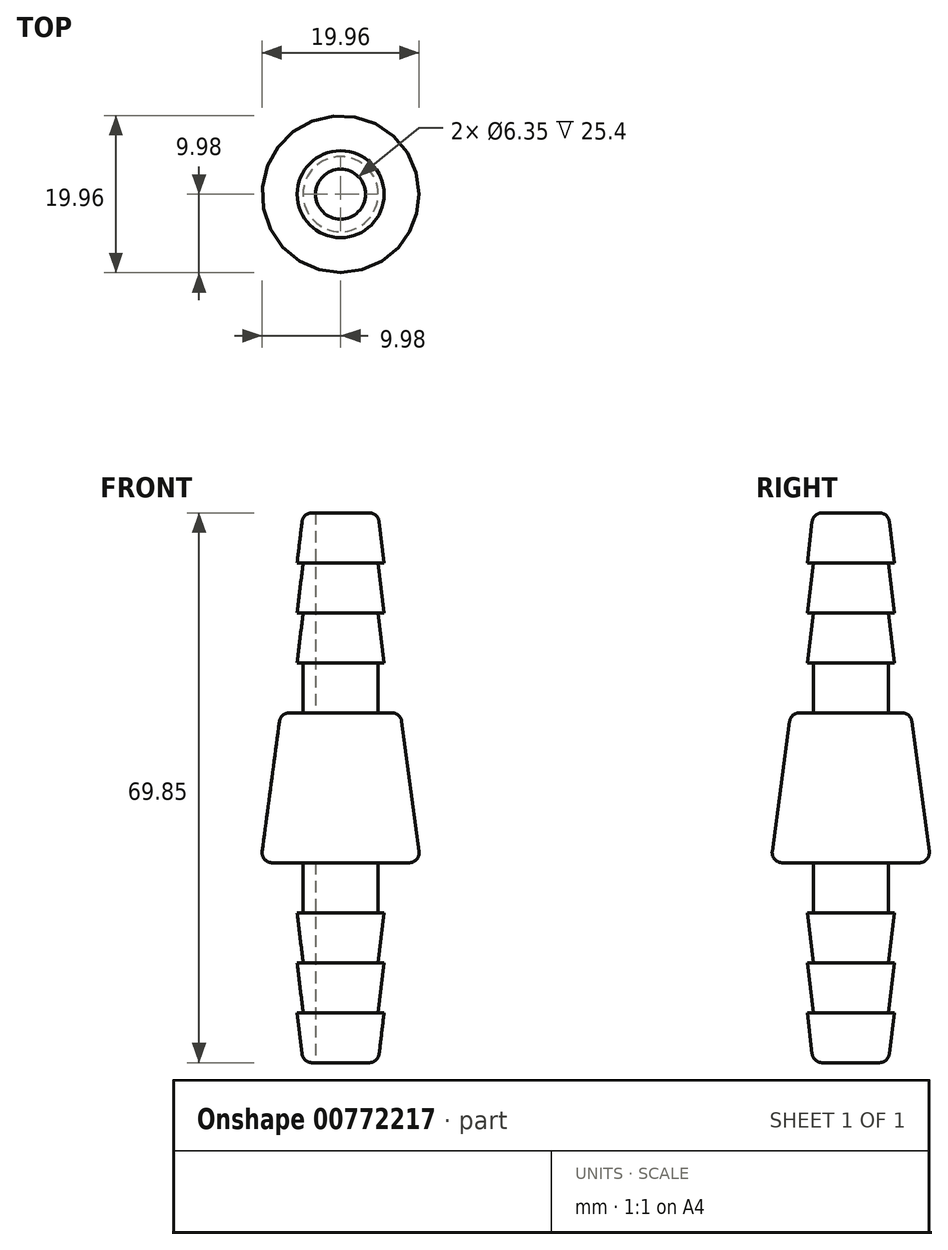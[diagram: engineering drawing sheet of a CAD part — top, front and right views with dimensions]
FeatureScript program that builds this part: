
annotation { "Feature Type Name" : "Feature", "Feature Type Description" : "" }
export const myFeature = defineFeature(function(context is Context, id is Id, definition is map)
    precondition{}
    {
        {
            var Q0;
            Q0=qCreatedBy(makeId("Front.planeOp"),FACE);
            var sketch = newSketch(context, id + "F0", { "sketchPlane" : qUnion([Q0])});
            skLineSegment(sketch, "E0", {"start": v(0, 0) * mm, "end": v(0, 69.85) * mm});
            skLineSegment(sketch, "E1", {"start": v(0, 34.93) * mm, "end": v(8.89, 34.93) * mm});
            skLineSegment(sketch, "E2", {"start": v(8.9, 34.93) * mm, "end": v(7.62, 44.45) * mm});
            skLineSegment(sketch, "E3", {"start": v(7.62, 44.45) * mm, "end": v(4.76, 44.45) * mm});
            skLineSegment(sketch, "E4", {"start": v(8.89, 34.93) * mm, "end": v(10.16, 25.4) * mm});
            skLineSegment(sketch, "E5", {"start": v(10.16, 25.4) * mm, "end": v(0, 25.4) * mm});
            skLineSegment(sketch, "E6", {"start": v(0, 44.45) * mm, "end": v(3.17, 44.45) * mm});
            skLineSegment(sketch, "E7", {"start": v(4.76, 44.45) * mm, "end": v(5.52, 44.45) * mm});
            skLineSegment(sketch, "E8", {"start": v(3.17, 44.45) * mm, "end": v(3.17, 69.85) * mm});
            skLineSegment(sketch, "E9", {"start": v(4.76, 44.45) * mm, "end": v(4.76, 50.8) * mm});
            skLineSegment(sketch, "E10", {"start": v(3.17, 69.85) * mm, "end": v(5.52, 69.85) * mm});
            skLineSegment(sketch, "E11", {"start": v(4.76, 50.8) * mm, "end": v(5.52, 50.8) * mm});
            skLineSegment(sketch, "E12", {"start": v(5.52, 50.8) * mm, "end": v(4.76, 57.15) * mm});
            skLineSegment(sketch, "E13", {"start": v(4.76, 57.15) * mm, "end": v(5.52, 57.15) * mm});
            skLineSegment(sketch, "E14", {"start": v(5.52, 57.15) * mm, "end": v(4.76, 63.5) * mm});
            skLineSegment(sketch, "E15", {"start": v(4.76, 63.5) * mm, "end": v(5.52, 63.5) * mm});
            skLineSegment(sketch, "E16", {"start": v(5.52, 63.5) * mm, "end": v(4.76, 69.85) * mm});
            skLineSegment(sketch, "E17.trimOffspring", {"start": v(3.17, 44.45) * mm, "end": v(0, 44.45) * mm});
            skLineSegment(sketch, "E18.MirrorCS", {"start": v(0, 25.4) * mm, "end": v(3.17, 25.4) * mm});
            skLineSegment(sketch, "E19.MirrorCS", {"start": v(4.76, 25.4) * mm, "end": v(5.52, 25.4) * mm});
            skLineSegment(sketch, "E20.MirrorCS", {"start": v(7.62, 25.4) * mm, "end": v(4.76, 25.4) * mm});
            skLineSegment(sketch, "E21.MirrorCS", {"start": v(3.17, 25.4) * mm, "end": v(0, 25.4) * mm});
            skLineSegment(sketch, "E22.MirrorCS", {"start": v(4.76, 19.05) * mm, "end": v(5.52, 19.05) * mm});
            skLineSegment(sketch, "E23.MirrorCS", {"start": v(3.17, 0) * mm, "end": v(5.52, 0) * mm});
            skLineSegment(sketch, "E24.MirrorCS", {"start": v(4.76, 6.35) * mm, "end": v(5.52, 6.35) * mm});
            skLineSegment(sketch, "E25.MirrorCS", {"start": v(4.76, 12.7) * mm, "end": v(5.52, 12.7) * mm});
            skLineSegment(sketch, "E26.MirrorCS", {"start": v(4.76, 25.4) * mm, "end": v(4.76, 19.05) * mm});
            skLineSegment(sketch, "E27.MirrorCS", {"start": v(3.17, 25.4) * mm, "end": v(3.17, 0) * mm});
            skLineSegment(sketch, "E28.MirrorCS", {"start": v(5.52, 12.7) * mm, "end": v(4.76, 6.35) * mm});
            skLineSegment(sketch, "E29.MirrorCS", {"start": v(5.52, 6.35) * mm, "end": v(4.76, 0) * mm});
            skLineSegment(sketch, "E30.MirrorCS", {"start": v(5.52, 19.05) * mm, "end": v(4.76, 12.7) * mm});
            skSolve(sketch);
        }
        {
            var Q0;
            Q0 = qSketchRegion(id + "F0", true);
            var Q1;
            Q1=sQuery(id+"F0.wireOp",EDGE,"E0");
            revolve(context, id + "F1", {"surfaceOperationType" : NewSurfaceOperationType.NEW, "entities" : qUnion([Q0]), "axis" : qUnion([Q1]), "revolveType" : RevolveType.FULL});
        }
        {
            var Q0;
            Q0=makeQuery(id+"F1.opRevolve","SWEPT_EDGE",EDGE,{"disambiguationData":[OSD([sQuery(id+"F0.wireOp",EDGE,"E4"),sQuery(id+"F0.wireOp",EDGE,"E5")])]});
            var Q1;
            Q1=makeQuery(id+"F1.opRevolve","SWEPT_EDGE",EDGE,{"disambiguationData":[OSD([sQuery(id+"F0.wireOp",EDGE,"E2"),sQuery(id+"F0.wireOp",EDGE,"E3")])]});
            var Q2;
            Q2=makeQuery(id+"F1.opRevolve","SWEPT_EDGE",EDGE,{"disambiguationData":[OSD([sQuery(id+"F0.wireOp",EDGE,"E10"),sQuery(id+"F0.wireOp",EDGE,"E16")])]});
            var Q3;
            Q3=makeQuery(id+"F1.opRevolve","SWEPT_EDGE",EDGE,{"disambiguationData":[OSD([sQuery(id+"F0.wireOp",EDGE,"E23.MirrorCS"),sQuery(id+"F0.wireOp",EDGE,"E29.MirrorCS")])]});
            fillet(context, id + "F2", {"entities" : qUnion([Q0, Q1, Q2, Q3]), "radius" : 1.27 * mm, "tangentPropagation" : true, "allowEdgeOverflow" : false});
        }
    });
